# Revit family: Toilet-Round-American_Standard-Triangle_Cadet_PRO-216BD104.020
name_source: partatom
category: Plumbing Fixtures
revit_build: Autodesk Revit 2018 (Build: 20170223_1515(x64)
units: mm (PartAtom-declared; Revit-internal decimal feet)

## family parameters
Always vertical = No
Cut with Voids When Loaded = No
OmniClass Number = 23.45.05.21.11.11
OmniClass Title = Water Operated Water Closets
Part Type = Normal
Room Calculation Point = No
Round Connector Dimension = Use Radius
Shared = Yes
Work Plane-Based = Yes

## types (1)
- 216BD104.020
    3517B.101 Right Height® Round Front Bowl = No
    4189D.104 Triangle Cadet PRO HET Tank = No
    5320.110 EverClean® Round Front Seat with Slow Close Snap-Off Hinges = No
    ADA Compliant = Yes
    Assembly Code = D2010110
    Bowl Shape = Round
    CEC Compliant = Yes
    CW Connection = Yes
    CWFU = 10
    CalGreen Compliant = Yes
    Cold Water Connection Diameter = 3/8"
    Cold Water Connection Height = 8"
    Cold Water Connection Radius = 3/16"
    Cold Water Connection Width = 6"
    Default Elevation = 0"
    Description = Triangle Cadet Pro Right Height Round Front Toilet
    Finish = Vitreous China-American Standard-020-White
    Flush Rate = 1.28 gpf (4.8 Lpf)
    HW Connection = No
    HWFU = 0
    Height = 32 1/16"
    IAPMO Compliance = Meets or Exceeds ASME A112.19.2-2008/CSA B45.1-08 for Vitreous China Fixtures
    Installation Type = Floor Mounted
    Length = 33 3/16"
    Manufacturer = American Standard
    Material = Vitreous China-American Standard-020-White
    Model = 216BD104.020
    Price = Prices may vary. Please consult Manufacturer Representative for most up-to-date price list.
    Product Documentation Link = https://americanstandard.box.com
    Product Page URL = https://www.americanstandard-us.com
    Revised Date = 03/09/2022
    URL = http://www.americanstandard-us.com
    Vent Connection = No
    WFU = 10
    Warranty Information = 5 Year (Limited)
    Waste Connection = Yes
    Waste Connection Diameter = 2 1/8"
    Waste Connection Radius = 1 1/16"
    Width = 19 3/8"

## geometry (parser evidence)
native form markers: Sweep x3
no freeform markers — native parametric forms only
